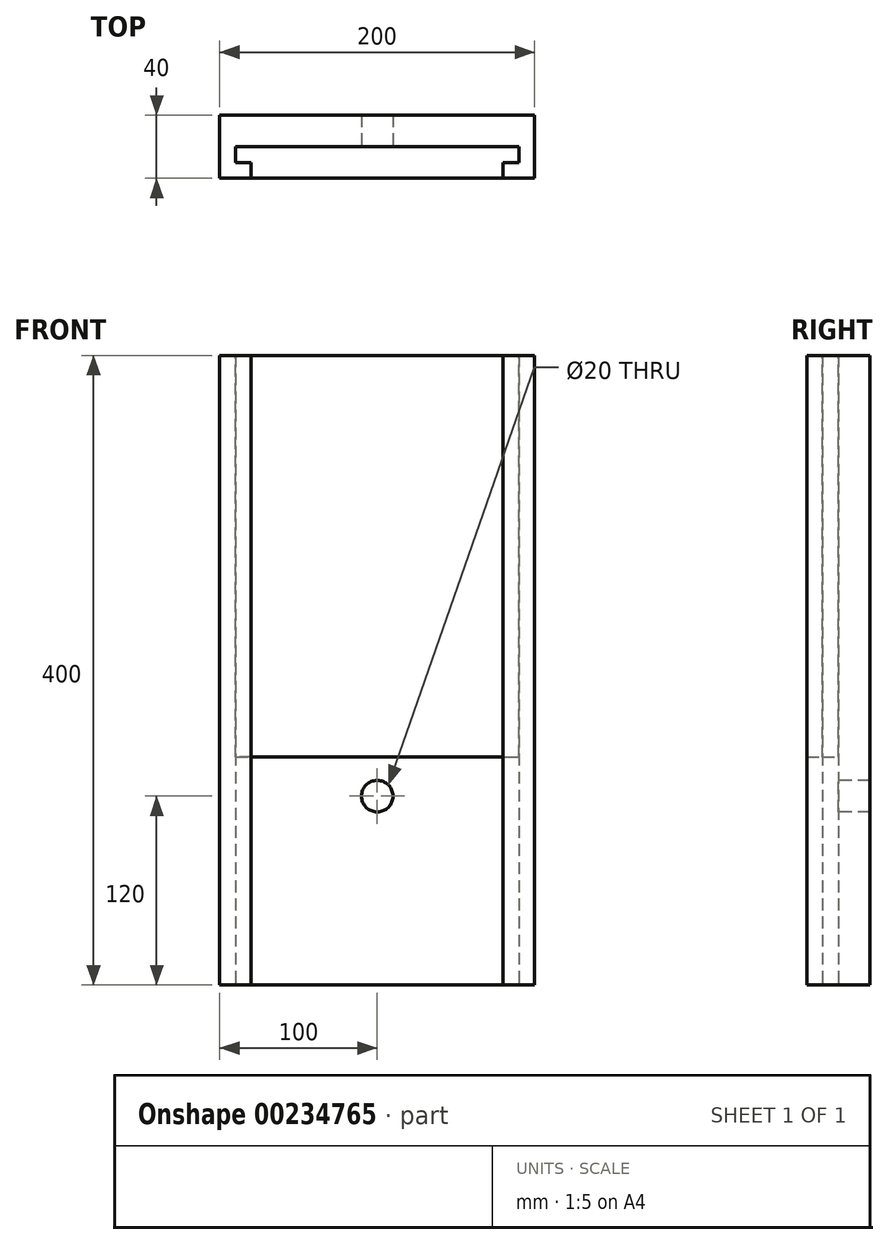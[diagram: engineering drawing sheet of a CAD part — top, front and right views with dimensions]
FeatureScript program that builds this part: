
annotation { "Feature Type Name" : "Feature", "Feature Type Description" : "" }
export const myFeature = defineFeature(function(context is Context, id is Id, definition is map)
    precondition{}
    {
        {
            var Q0;
            Q0=qCreatedBy(makeId("Top.planeOp"),FACE);
            var sketch = newSketch(context, id + "F0", { "sketchPlane" : qUnion([Q0])});
            skLineSegment(sketch, "E0", {"start": v(0, 40) * mm, "end": v(100, 40) * mm});
            skLineSegment(sketch, "E1", {"start": v(100, 40) * mm, "end": v(100, 0) * mm});
            skLineSegment(sketch, "E2", {"start": v(100, 0) * mm, "end": v(80, 0) * mm});
            skLineSegment(sketch, "E3", {"start": v(80, 0) * mm, "end": v(80, 10) * mm});
            skLineSegment(sketch, "E4", {"start": v(80, 10) * mm, "end": v(90, 10) * mm});
            skLineSegment(sketch, "E5", {"start": v(90, 10) * mm, "end": v(90, 20) * mm});
            skLineSegment(sketch, "E6", {"start": v(90, 20) * mm, "end": v(0, 20) * mm});
            skLineSegment(sketch, "E7", {"start": v(0, 40) * mm, "end": v(0, 0) * mm, "construction": true});
            skLineSegment(sketch, "E8.MirrorCS", {"start": v(-100, 40) * mm, "end": v(-100, 0) * mm});
            skLineSegment(sketch, "E9.MirrorCS", {"start": v(-90, 10) * mm, "end": v(-90, 20) * mm});
            skLineSegment(sketch, "E10.MirrorCS", {"start": v(0, 40) * mm, "end": v(-100, 40) * mm});
            skLineSegment(sketch, "E11.MirrorCS", {"start": v(-80, 10) * mm, "end": v(-90, 10) * mm});
            skLineSegment(sketch, "E12.MirrorCS", {"start": v(-80, 0) * mm, "end": v(-80, 10) * mm});
            skLineSegment(sketch, "E13.MirrorCS", {"start": v(-100, 0) * mm, "end": v(-80, 0) * mm});
            skLineSegment(sketch, "E14.MirrorCS", {"start": v(-90, 20) * mm, "end": v(0, 20) * mm});
            skSolve(sketch);
        }
        {
            var Q0;
            Q0 = qSketchRegion(id + "F0", true);
            extrude(context, id + "F1", {"entities" : qUnion([Q0]), "depth" : 280 * mm, "hasSecondDirection" : true, "secondDirectionOppositeDirection" : true, "secondDirectionDepth" : 120 * mm});
        }
        {
            var Q0;
            Q0=makeQuery(id+"F1.opExtrude","SWEPT_FACE",FACE,{"disambiguationData":[OSD([sQuery(id+"F0.wireOp",EDGE,"E6"),sQuery(id+"F0.wireOp",EDGE,"E14.MirrorCS")])]});
            var sketch = newSketch(context, id + "F2", { "sketchPlane" : qUnion([Q0])});
            skCircle(sketch, "E15", {"center": v(0, 0) * mm, "radius": 10 * mm});
            skSolve(sketch);
        }
        {
            var Q0;
            Q0 = qSketchRegion(id + "F2", true);
            extrude(context, id + "F3", {"entities" : qUnion([Q0]), "operationType" : NewBodyOperationType.REMOVE, "endBound" : BoundingType.THROUGH_ALL, "oppositeDirection" : true, "depth" : 25 * mm});
        }
        {
            var Q0;
            Q0=makeQuery(id+"F1.opExtrude","CAP_FACE",FACE,{"disambiguationData":[OSD([sQuery(id+"F0.wireOp",EDGE,"E0"),sQuery(id+"F0.wireOp",EDGE,"E1"),sQuery(id+"F0.wireOp",EDGE,"E2"),sQuery(id+"F0.wireOp",EDGE,"E3"),sQuery(id+"F0.wireOp",EDGE,"E4"),sQuery(id+"F0.wireOp",EDGE,"E5"),sQuery(id+"F0.wireOp",EDGE,"E6"),sQuery(id+"F0.wireOp",EDGE,"E8.MirrorCS"),sQuery(id+"F0.wireOp",EDGE,"E9.MirrorCS"),sQuery(id+"F0.wireOp",EDGE,"E10.MirrorCS"),sQuery(id+"F0.wireOp",EDGE,"E11.MirrorCS"),sQuery(id+"F0.wireOp",EDGE,"E12.MirrorCS"),sQuery(id+"F0.wireOp",EDGE,"E13.MirrorCS"),sQuery(id+"F0.wireOp",EDGE,"E14.MirrorCS")])],"isStart":false});
            var sketch = newSketch(context, id + "F4", { "sketchPlane" : qUnion([Q0])});
            skLineSegment(sketch, "E16", {"start": v(90, 20) * mm, "end": v(90, 10) * mm});
            skLineSegment(sketch, "E17", {"start": v(90, 10) * mm, "end": v(80, 10) * mm});
            skLineSegment(sketch, "E18", {"start": v(80, 10) * mm, "end": v(80, 0) * mm});
            skLineSegment(sketch, "E19", {"start": v(80, 0) * mm, "end": v(-80, 0) * mm});
            skLineSegment(sketch, "E20", {"start": v(-80, 0) * mm, "end": v(-80, 10) * mm});
            skLineSegment(sketch, "E21", {"start": v(-80, 10) * mm, "end": v(-90, 10) * mm});
            skLineSegment(sketch, "E22", {"start": v(-90, 10) * mm, "end": v(-90, 20) * mm});
            skLineSegment(sketch, "E23", {"start": v(-90, 20) * mm, "end": v(90, 20) * mm});
            skSolve(sketch);
        }
        {
            var Q0;
            Q0 = qSketchRegion(id + "F4", true);
            extrude(context, id + "F5", {"entities" : qUnion([Q0]), "oppositeDirection" : true, "depth" : 255 * mm});
        }
    });
